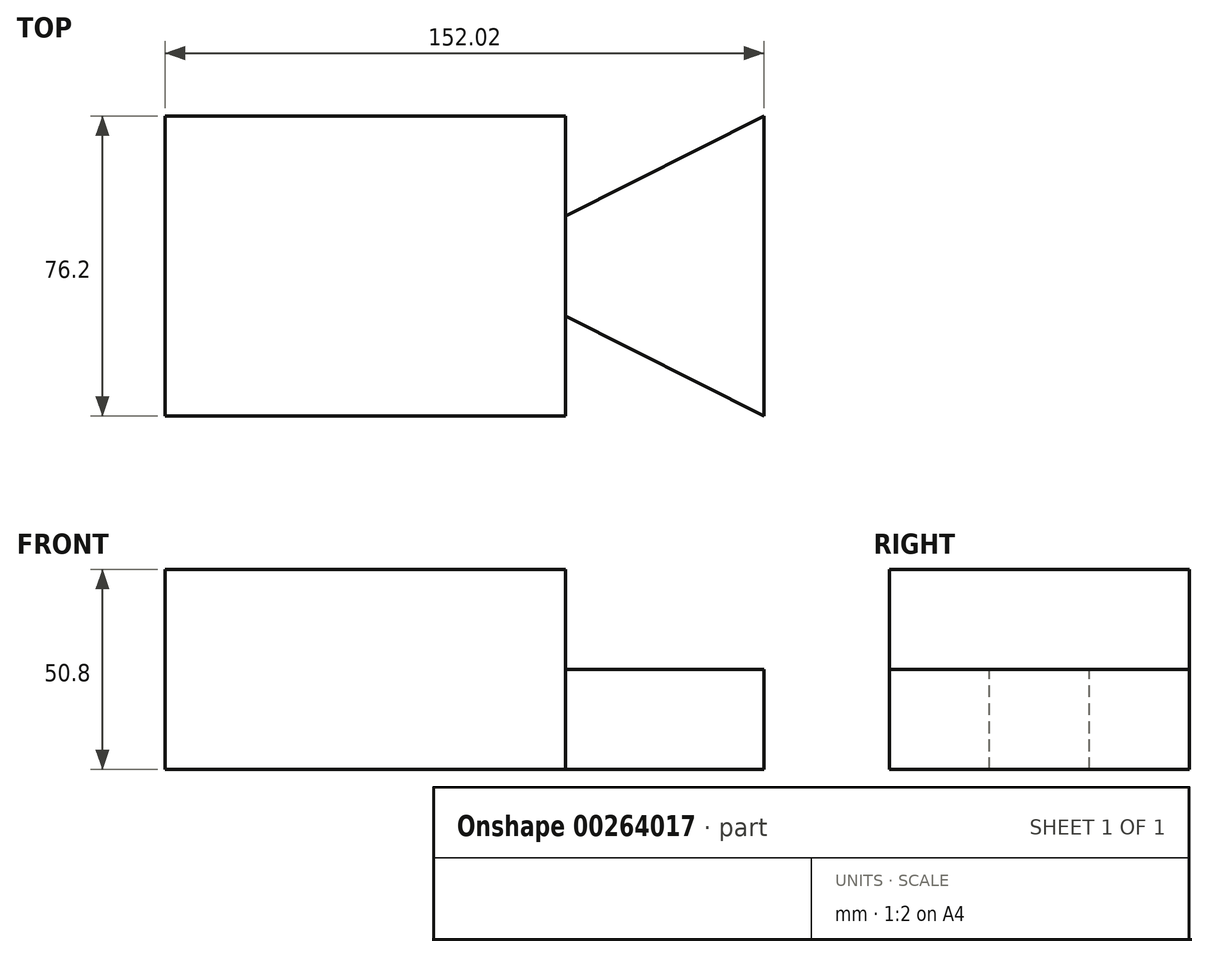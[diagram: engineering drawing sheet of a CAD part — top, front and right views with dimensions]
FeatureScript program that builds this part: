
annotation { "Feature Type Name" : "Feature", "Feature Type Description" : "" }
export const myFeature = defineFeature(function(context is Context, id is Id, definition is map)
    precondition{}
    {
        {
            var Q0;
            Q0=qCreatedBy(makeId("Top.planeOp"),FACE);
            var sketch = newSketch(context, id + "F0", { "sketchPlane" : qUnion([Q0])});
            skLineSegment(sketch, "E0", {"start": v(-76.68, 50.8) * mm, "end": v(-76.68, -25.4) * mm});
            skLineSegment(sketch, "E1", {"start": v(-76.68, -25.4) * mm, "end": v(24.92, -25.4) * mm});
            skLineSegment(sketch, "E2", {"start": v(24.92, -25.4) * mm, "end": v(24.92, 0) * mm});
            skLineSegment(sketch, "E3", {"start": v(-76.68, 50.8) * mm, "end": v(24.92, 50.8) * mm});
            skLineSegment(sketch, "E4", {"start": v(24.92, 50.8) * mm, "end": v(24.92, 25.4) * mm});
            skLineSegment(sketch, "E5", {"start": v(24.92, 25.4) * mm, "end": v(75.34, 50.8) * mm});
            skLineSegment(sketch, "E6", {"start": v(75.34, 50.8) * mm, "end": v(75.34, -25.4) * mm});
            skLineSegment(sketch, "E7", {"start": v(75.34, -25.4) * mm, "end": v(24.92, 0) * mm});
            skLineSegment(sketch, "E8", {"start": v(24.92, 25.4) * mm, "end": v(24.92, 0) * mm});
            skSolve(sketch);
        }
        {
            var Q0;
            Q0=makeQuery(id+"F0.imprint","IMPRINT",FACE,{"disambiguationData":[TD([[makeQuery(id+"F0.imprint","IMPRINT",EDGE,{"derivedFrom":sQuery(id+"F0.wireOp",EDGE,"E0")}),1.0]])]});
            extrude(context, id + "F1", {"entities" : qUnion([Q0]), "depth" : 25.4 * mm});
        }
        {
            var Q0;
            Q0=makeQuery(id+"F0.imprint","IMPRINT",FACE,{"disambiguationData":[TD([[makeQuery(id+"F0.imprint","IMPRINT",EDGE,{"derivedFrom":sQuery(id+"F0.wireOp",EDGE,"E5")}),-1.0]])]});
            extrude(context, id + "F2", {"entities" : qUnion([Q0]), "operationType" : NewBodyOperationType.ADD, "oppositeDirection" : true, "depth" : 25.4 * mm});
        }
        {
            var Q0;
            Q0=makeQuery(id+"F0.imprint","IMPRINT",FACE,{"disambiguationData":[TD([[makeQuery(id+"F0.imprint","IMPRINT",EDGE,{"derivedFrom":sQuery(id+"F0.wireOp",EDGE,"E0")}),1.0]])]});
            extrude(context, id + "F3", {"entities" : qUnion([Q0]), "operationType" : NewBodyOperationType.ADD, "oppositeDirection" : true, "depth" : 25.4 * mm});
        }
        {
            var Q0;
            Q0=makeQuery(id+"F0.imprint","IMPRINT",FACE,{"disambiguationData":[TD([[makeQuery(id+"F0.imprint","IMPRINT",EDGE,{"derivedFrom":sQuery(id+"F0.wireOp",EDGE,"E5")}),-1.0]])]});
            extrude(context, id + "F4", {"entities" : qUnion([Q0]), "operationType" : NewBodyOperationType.ADD, "oppositeDirection" : true, "depth" : 24.9 * mm});
        }
    });
